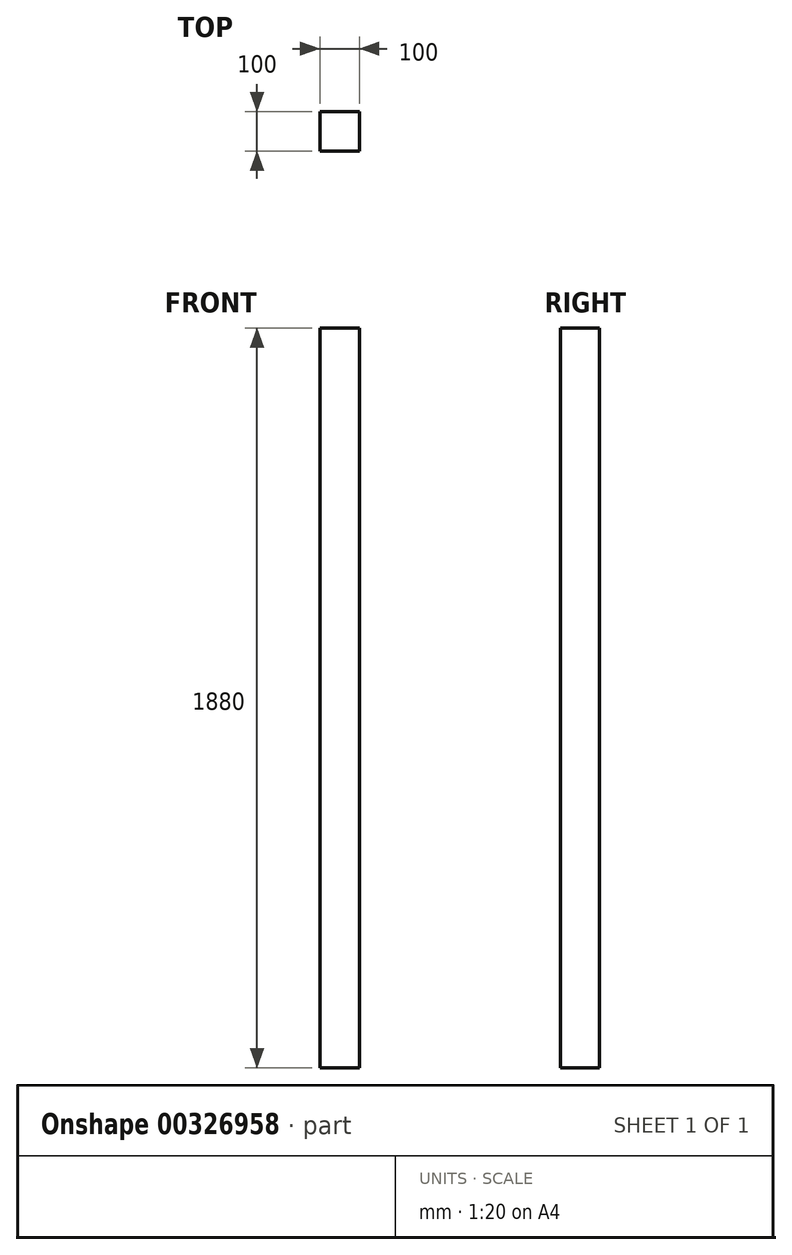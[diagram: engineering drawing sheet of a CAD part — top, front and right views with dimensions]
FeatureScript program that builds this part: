
annotation { "Feature Type Name" : "Feature", "Feature Type Description" : "" }
export const myFeature = defineFeature(function(context is Context, id is Id, definition is map)
    precondition{}
    {
        {
            var Q0;
            Q0=qCreatedBy(makeId("Top.planeOp"),FACE);
            var sketch = newSketch(context, id + "F0", { "sketchPlane" : qUnion([Q0])});
            skLineSegment(sketch, "E0.bottom", {"start": v(-50, -50) * mm, "end": v(50, -50) * mm});
            skLineSegment(sketch, "E0.top", {"start": v(-50, 50) * mm, "end": v(50, 50) * mm});
            skLineSegment(sketch, "E0.left", {"start": v(-50, -50) * mm, "end": v(-50, 50) * mm});
            skLineSegment(sketch, "E0.right", {"start": v(50, -50) * mm, "end": v(50, 50) * mm});
            skPoint(sketch, "E0.middle", {"position": v(0, 0) * mm});
            skSolve(sketch);
        }
        {
            var Q0;
            Q0 = qSketchRegion(id + "F0", true);
            extrude(context, id + "F1", {"entities" : qUnion([Q0]), "depth" : 1880 * mm});
        }
    });
